# Revit family: DOKSTAR
name_source: partatom
category: Lighting Fixtures
units: mm (PartAtom-declared; Revit-internal decimal feet)

## family parameters
Cut with Voids When Loaded = No
Host = Face
Light Source = No
OmniClass Number = 23.80.70.11
OmniClass Title = Luminaries for Internal Lighting
Part Type = Normal
Room Calculation Point = No
Round Connector Dimension = Use Diameter
Shared = Yes

## types (1)
- DOK
    Apparent Load = 0 VA
    Assembly Code = D5020200
    Default Elevation = 4' - 0"
    Description = LED Freight Loading Dock Fixture
    Fastener = Steel
    Glass = White Glass
    Housing Material = Powdercoat- Yellow
    Lamp = LED's
    Load Classification = Lighting
    Manufacturer = Columbia Lighting
    Model = DOK
    Power Factor = 1
    Product Name = Dokstar
    URL = https://www.currentlighting.com
    Voltage = 120 V
    Wattage Comments = Up to 131 lumens/watt efficacy

## geometry (parser evidence)
native form markers: Sweep x14
no freeform markers — native parametric forms only
